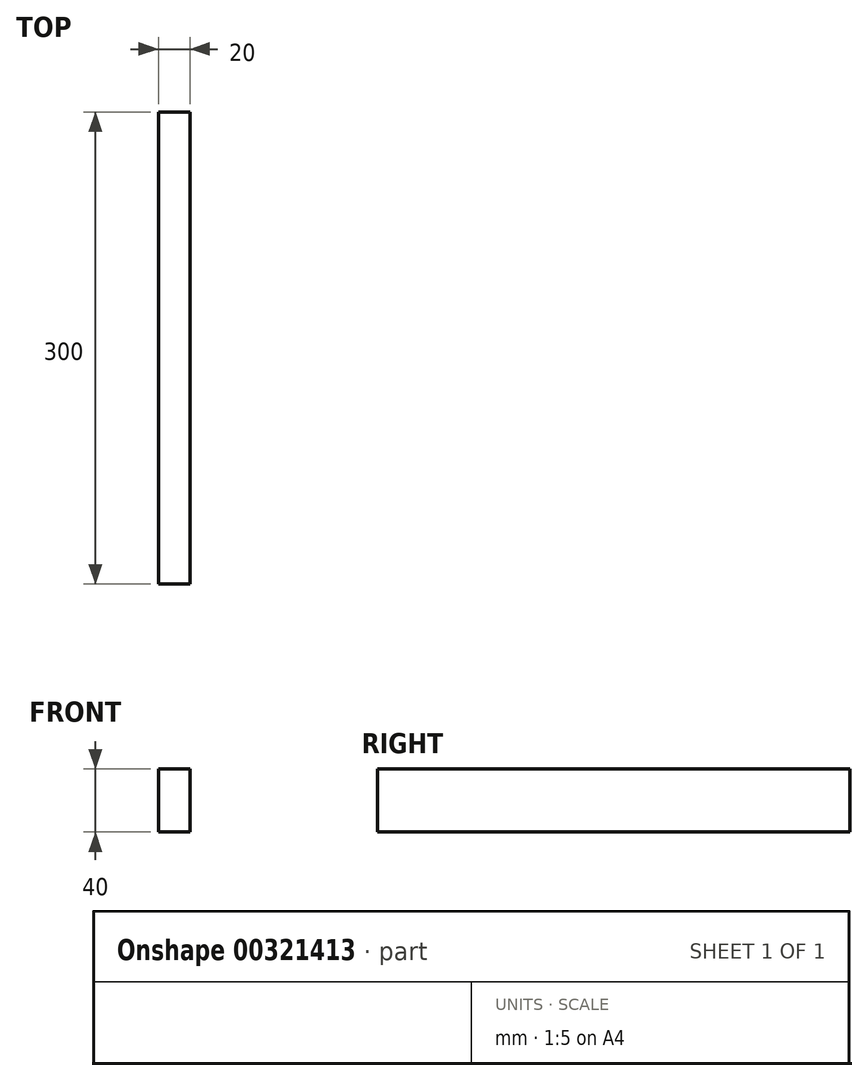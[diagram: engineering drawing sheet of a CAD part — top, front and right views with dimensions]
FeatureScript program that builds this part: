
annotation { "Feature Type Name" : "Feature", "Feature Type Description" : "" }
export const myFeature = defineFeature(function(context is Context, id is Id, definition is map)
    precondition{}
    {
        {
            var Q0;
            Q0=qCreatedBy(makeId("Front.planeOp"),FACE);
            var sketch = newSketch(context, id + "F0", { "sketchPlane" : qUnion([Q0])});
            skLineSegment(sketch, "E0.bottom", {"start": v(10, -20) * mm, "end": v(-10, -20) * mm});
            skLineSegment(sketch, "E0.top", {"start": v(10, 20) * mm, "end": v(-10, 20) * mm});
            skLineSegment(sketch, "E0.left", {"start": v(10, -20) * mm, "end": v(10, 20) * mm});
            skLineSegment(sketch, "E0.right", {"start": v(-10, -20) * mm, "end": v(-10, 20) * mm});
            skPoint(sketch, "E0.middle", {"position": v(0, 0) * mm});
            skSolve(sketch);
        }
        {
            var Q0;
            Q0=makeQuery(id+"F0.imprint","IMPRINT",FACE,{"disambiguationData":[TD([[makeQuery(id+"F0.imprint","IMPRINT",EDGE,{"derivedFrom":sQuery(id+"F0.wireOp",EDGE,"E0.bottom")}),-1.0]])]});
            extrude(context, id + "F1", {"entities" : qUnion([Q0]), "depth" : 300 * mm});
        }
    });
